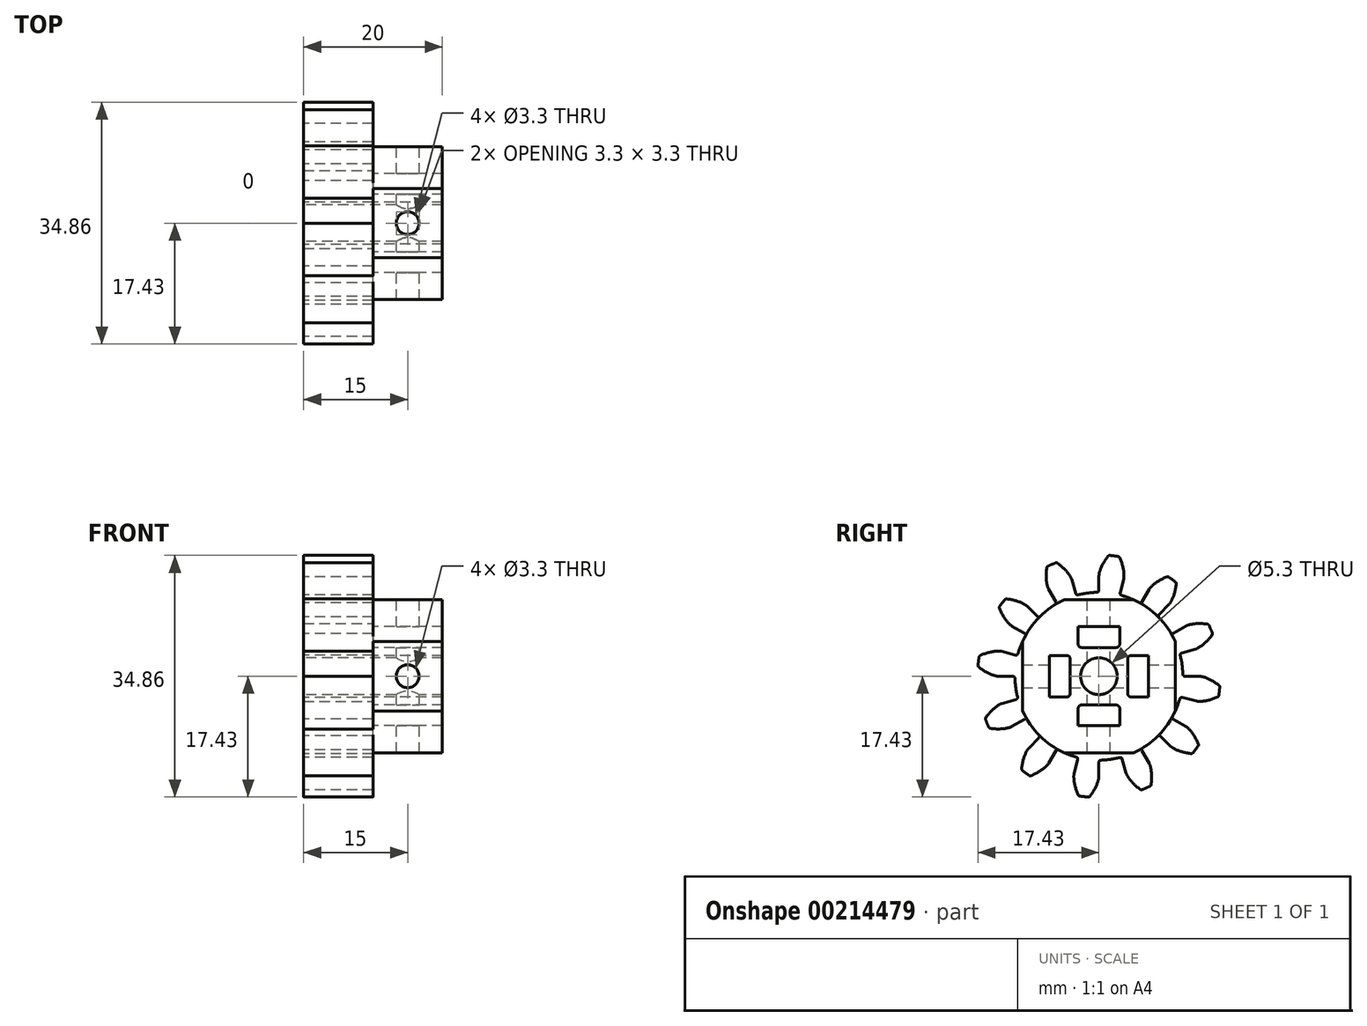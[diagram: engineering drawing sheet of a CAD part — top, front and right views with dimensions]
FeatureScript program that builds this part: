
annotation { "Feature Type Name" : "Feature", "Feature Type Description" : "" }
export const myFeature = defineFeature(function(context is Context, id is Id, definition is map)
    precondition{}
    {
        {
            assignVariable(context, id + "F0", {"name" : "NumberTeeth", "anyValue" : 12});
        }
        {
            assignVariable(context, id + "F1", {"name" : "GearThickness", "anyValue" : 10});
        }
        {
            var Q0;
            Q0=qCreatedBy(makeId("Right.planeOp"),FACE);
            var sketch = newSketch(context, id + "F2", { "sketchPlane" : qUnion([Q0])});
            skCircle(sketch, "E0", {"center": v(0, 0) * mm, "radius": 12.1 * mm});
            skCircle(sketch, "E1", {"center": v(0, 0) * mm, "radius": 14.52 * mm, "construction": true});
            skCircle(sketch, "E2", {"center": v(0, 0) * mm, "radius": 15 * mm, "construction": true});
            skCircle(sketch, "E3", {"center": v(0, 0) * mm, "radius": 17.5 * mm});
            skLineSegment(sketch, "E4", {"start": v(0, 0) * mm, "end": v(-14.52, 0) * mm, "construction": true});
            skLineSegment(sketch, "E5.1.0", {"start": v(0, 0) * mm, "end": v(-14.5, 0.73) * mm, "construction": true});
            skLineSegment(sketch, "E5.2.0", {"start": v(0, 0) * mm, "end": v(-14.45, 1.45) * mm, "construction": true});
            skLineSegment(sketch, "E5.3.0", {"start": v(0, 0) * mm, "end": v(-14.36, 2.17) * mm, "construction": true});
            skLineSegment(sketch, "E5.4.0", {"start": v(0, 0) * mm, "end": v(-14.23, 2.89) * mm, "construction": true});
            skLineSegment(sketch, "E5.5.0", {"start": v(0, 0) * mm, "end": v(-14.07, 3.6) * mm, "construction": true});
            skLineSegment(sketch, "E5.6.0", {"start": v(0, 0) * mm, "end": v(-13.87, 4.3) * mm, "construction": true});
            skLineSegment(sketch, "E5.7.0", {"start": v(0, 0) * mm, "end": v(-13.64, 4.98) * mm, "construction": true});
            skLineSegment(sketch, "E5.8.0", {"start": v(0, 0) * mm, "end": v(-13.38, 5.66) * mm, "construction": true});
            skLineSegment(sketch, "E5.9.0", {"start": v(0, 0) * mm, "end": v(-13.08, 6.32) * mm, "construction": true});
            skLineSegment(sketch, "E5.10.0", {"start": v(0, 0) * mm, "end": v(-12.74, 6.96) * mm, "construction": true});
            skLineSegment(sketch, "E5.11.0", {"start": v(0, 0) * mm, "end": v(-12.38, 7.6) * mm, "construction": true});
            skLineSegment(sketch, "E5.12.0", {"start": v(0, 0) * mm, "end": v(-11.99, 8.2) * mm, "construction": true});
            skLineSegment(sketch, "E5.13.0", {"start": v(0, 0) * mm, "end": v(-11.56, 8.79) * mm, "construction": true});
            skLineSegment(sketch, "E5.14.0", {"start": v(0, 0) * mm, "end": v(-11.1, 9.36) * mm, "construction": true});
            skLineSegment(sketch, "E5.anchor2", {"start": v(0, 0) * mm, "end": v(-11.1, 9.36) * mm, "construction": true});
            skLineSegment(sketch, "E6", {"start": v(-14.5, 0.73) * mm, "end": v(-14.54, 0) * mm, "construction": true});
            skLineSegment(sketch, "E7", {"start": v(-14.45, 1.45) * mm, "end": v(-14.6, 0) * mm, "construction": true});
            skLineSegment(sketch, "E8", {"start": v(-14.36, 2.17) * mm, "end": v(-14.68, 0.02) * mm, "construction": true});
            skLineSegment(sketch, "E9", {"start": v(-14.07, 3.6) * mm, "end": v(-14.97, 0.08) * mm, "construction": true});
            skLineSegment(sketch, "E10", {"start": v(-13.87, 4.3) * mm, "end": v(-15.16, 0.13) * mm, "construction": true});
            skLineSegment(sketch, "E11", {"start": v(-13.64, 4.98) * mm, "end": v(-15.38, 0.2) * mm, "construction": true});
            skLineSegment(sketch, "E12", {"start": v(-13.38, 5.66) * mm, "end": v(-15.64, 0.3) * mm, "construction": true});
            skLineSegment(sketch, "E13", {"start": v(-13.08, 6.32) * mm, "end": v(-15.92, 0.43) * mm, "construction": true});
            skLineSegment(sketch, "E14", {"start": v(-12.74, 6.96) * mm, "end": v(-16.23, 0.6) * mm, "construction": true});
            skLineSegment(sketch, "E15", {"start": v(-12.38, 7.6) * mm, "end": v(-16.56, 0.78) * mm, "construction": true});
            skLineSegment(sketch, "E16", {"start": v(-14.23, 2.89) * mm, "end": v(-14.8, 0.04) * mm, "construction": true});
            skLineSegment(sketch, "E17", {"start": v(-11.99, 8.2) * mm, "end": v(-16.9, 1) * mm, "construction": true});
            skLineSegment(sketch, "E18", {"start": v(-11.56, 8.79) * mm, "end": v(-17.27, 1.27) * mm, "construction": true});
            skLineSegment(sketch, "E19", {"start": v(-11.1, 9.36) * mm, "end": v(-17.66, 1.58) * mm, "construction": true});
            skLineSegment(sketch, "E20", {"start": v(0, 0) * mm, "end": v(-14.4, 1.8) * mm, "construction": true});
            skLineSegment(sketch, "E21", {"start": v(-12.1, 0) * mm, "end": v(-14.52, 0) * mm});
            skLineSegment(sketch, "E22.MirrorCS", {"start": v(-11.73, 2.99) * mm, "end": v(-14.07, 3.58) * mm});
            skLineSegment(sketch, "E23", {"start": v(-17.66, 1.58) * mm, "end": v(-17.84, 1.74) * mm, "construction": true});
            skFitSpline(sketch, "E24", {"points": [v(-17.66, 1.58) * mm, v(-17.27, 1.27) * mm, v(-16.9, 1) * mm, v(-16.56, 0.78) * mm, v(-16.23, 0.6) * mm, v(-15.92, 0.43) * mm, v(-15.64, 0.3) * mm, v(-15.38, 0.2) * mm, v(-15.16, 0.13) * mm, v(-14.97, 0.08) * mm, v(-14.8, 0.04) * mm, v(-14.68, 0.02) * mm, v(-14.6, 0) * mm, v(-14.54, 0) * mm, v(-14.52, 0) * mm], "startDerivative": vector(2.51, -2.05) * mm, "endDerivative": vector(1.04, 0) * mm});
            skFitSpline(sketch, "E25.MirrorCS", {"points": [v(-17.5, 2.83) * mm, v(-17.05, 3.03) * mm, v(-16.63, 3.2) * mm, v(-16.24, 3.33) * mm, v(-15.87, 3.43) * mm, v(-15.53, 3.5) * mm, v(-15.23, 3.56) * mm, v(-14.96, 3.6) * mm, v(-14.72, 3.62) * mm, v(-14.52, 3.62) * mm, v(-14.36, 3.62) * mm, v(-14.23, 3.6) * mm, v(-14.14, 3.6) * mm, v(-14.1, 3.59) * mm, v(-14.07, 3.58) * mm], "startDerivative": vector(2.94, 1.36) * mm, "endDerivative": vector(1.01, -0.26) * mm});
            skSolve(sketch);
        }
        {
            var Q0;
            {var subQ0=sQuery(id+"F2.wireOp",EDGE,"E0");var subQ27=makeQuery(id+"F2.imprint","INTERSECT",VERTEX,{"derivedFrom":[subQ0,sQuery(id+"F2.wireOp",EDGE,"10ea1024-8cf5-41f5-a75f-a634b86921f3.10.0")]});Q0=makeQuery(id+"F2.imprint","IMPRINT",FACE,{"disambiguationData":[TD([[makeQuery(id+"F2.imprint","IMPRINT",EDGE,{"disambiguationData":[TD([[subQ27,-1.0]])],"derivedFrom":subQ0}),1.0]])]});}
            var Q1;
            {var subQ0=sQuery(id+"F2.wireOp",EDGE,"10ea1024-8cf5-41f5-a75f-a634b86921f3.1.0");Q1=makeQuery(id+"F2.imprint","IMPRINT",FACE,{"disambiguationData":[TD([[makeQuery(id+"F2.imprint","IMPRINT",EDGE,{"derivedFrom":subQ0}),-1.0]])]});}
            var Q2;
            {var subQ7=sQuery(id+"F2.wireOp",EDGE,"10ea1024-8cf5-41f5-a75f-a634b86921f3.2.0");Q2=makeQuery(id+"F2.imprint","IMPRINT",FACE,{"disambiguationData":[TD([[makeQuery(id+"F2.imprint","IMPRINT",EDGE,{"derivedFrom":subQ7}),-1.0]])]});}
            var Q3;
            {var subQ8=sQuery(id+"F2.wireOp",EDGE,"10ea1024-8cf5-41f5-a75f-a634b86921f3.3.0");Q3=makeQuery(id+"F2.imprint","IMPRINT",FACE,{"disambiguationData":[TD([[makeQuery(id+"F2.imprint","IMPRINT",EDGE,{"derivedFrom":subQ8}),-1.0]])]});}
            var Q4;
            {var subQ2=sQuery(id+"F2.wireOp",EDGE,"10ea1024-8cf5-41f5-a75f-a634b86921f3.4.0");Q4=makeQuery(id+"F2.imprint","IMPRINT",FACE,{"disambiguationData":[TD([[makeQuery(id+"F2.imprint","IMPRINT",EDGE,{"derivedFrom":subQ2}),-1.0]])]});}
            var Q5;
            {var subQ8=sQuery(id+"F2.wireOp",EDGE,"10ea1024-8cf5-41f5-a75f-a634b86921f3.5.0");Q5=makeQuery(id+"F2.imprint","IMPRINT",FACE,{"disambiguationData":[TD([[makeQuery(id+"F2.imprint","IMPRINT",EDGE,{"derivedFrom":subQ8}),-1.0]])]});}
            var Q6;
            {var subQ3=sQuery(id+"F2.wireOp",EDGE,"10ea1024-8cf5-41f5-a75f-a634b86921f3.6.0");Q6=makeQuery(id+"F2.imprint","IMPRINT",FACE,{"disambiguationData":[TD([[makeQuery(id+"F2.imprint","IMPRINT",EDGE,{"derivedFrom":subQ3}),-1.0]])]});}
            var Q7;
            {var subQ0=sQuery(id+"F2.wireOp",EDGE,"10ea1024-8cf5-41f5-a75f-a634b86921f3.7.0");Q7=makeQuery(id+"F2.imprint","IMPRINT",FACE,{"disambiguationData":[TD([[makeQuery(id+"F2.imprint","IMPRINT",EDGE,{"derivedFrom":subQ0}),-1.0]])]});}
            var Q8;
            {var subQ5=sQuery(id+"F2.wireOp",EDGE,"10ea1024-8cf5-41f5-a75f-a634b86921f3.8.0");Q8=makeQuery(id+"F2.imprint","IMPRINT",FACE,{"disambiguationData":[TD([[makeQuery(id+"F2.imprint","IMPRINT",EDGE,{"derivedFrom":subQ5}),-1.0]])]});}
            var Q9;
            {var subQ1=sQuery(id+"F2.wireOp",EDGE,"10ea1024-8cf5-41f5-a75f-a634b86921f3.9.0");Q9=makeQuery(id+"F2.imprint","IMPRINT",FACE,{"disambiguationData":[TD([[makeQuery(id+"F2.imprint","IMPRINT",EDGE,{"derivedFrom":subQ1}),-1.0]])]});}
            var Q10;
            {var subQ5=sQuery(id+"F2.wireOp",EDGE,"10ea1024-8cf5-41f5-a75f-a634b86921f3.10.0");Q10=makeQuery(id+"F2.imprint","IMPRINT",FACE,{"disambiguationData":[TD([[makeQuery(id+"F2.imprint","IMPRINT",EDGE,{"derivedFrom":subQ5}),-1.0]])]});}
            var Q11;
            {var subQ8=sQuery(id+"F2.wireOp",EDGE,"10ea1024-8cf5-41f5-a75f-a634b86921f3.11.0");Q11=makeQuery(id+"F2.imprint","IMPRINT",FACE,{"disambiguationData":[TD([[makeQuery(id+"F2.imprint","IMPRINT",EDGE,{"derivedFrom":subQ8}),-1.0]])]});}
            var Q12;
            {var subQ2=sQuery(id+"F2.wireOp",EDGE,"10ea1024-8cf5-41f5-a75f-a634b86921f3.12.0");Q12=makeQuery(id+"F2.imprint","IMPRINT",FACE,{"disambiguationData":[TD([[makeQuery(id+"F2.imprint","IMPRINT",EDGE,{"derivedFrom":subQ2}),-1.0]])]});}
            var Q13;
            {var subQ3=sQuery(id+"F2.wireOp",EDGE,"10ea1024-8cf5-41f5-a75f-a634b86921f3.13.0");Q13=makeQuery(id+"F2.imprint","IMPRINT",FACE,{"disambiguationData":[TD([[makeQuery(id+"F2.imprint","IMPRINT",EDGE,{"derivedFrom":subQ3}),-1.0]])]});}
            var Q14;
            {var subQ0=sQuery(id+"F2.wireOp",EDGE,"10ea1024-8cf5-41f5-a75f-a634b86921f3.14.0");Q14=makeQuery(id+"F2.imprint","IMPRINT",FACE,{"disambiguationData":[TD([[makeQuery(id+"F2.imprint","IMPRINT",EDGE,{"derivedFrom":subQ0}),-1.0]])]});}
            var Q15;
            {var subQ6=sQuery(id+"F2.wireOp",EDGE,"10ea1024-8cf5-41f5-a75f-a634b86921f3.15.0");Q15=makeQuery(id+"F2.imprint","IMPRINT",FACE,{"disambiguationData":[TD([[makeQuery(id+"F2.imprint","IMPRINT",EDGE,{"derivedFrom":subQ6}),-1.0]])]});}
            var Q16;
            {var subQ5=sQuery(id+"F2.wireOp",EDGE,"10ea1024-8cf5-41f5-a75f-a634b86921f3.16.0");Q16=makeQuery(id+"F2.imprint","IMPRINT",FACE,{"disambiguationData":[TD([[makeQuery(id+"F2.imprint","IMPRINT",EDGE,{"derivedFrom":subQ5}),-1.0]])]});}
            var Q17;
            {var subQ7=sQuery(id+"F2.wireOp",EDGE,"10ea1024-8cf5-41f5-a75f-a634b86921f3.17.0");Q17=makeQuery(id+"F2.imprint","IMPRINT",FACE,{"disambiguationData":[TD([[makeQuery(id+"F2.imprint","IMPRINT",EDGE,{"derivedFrom":subQ7}),-1.0]])]});}
            var Q18;
            {var subQ5=sQuery(id+"F2.wireOp",EDGE,"10ea1024-8cf5-41f5-a75f-a634b86921f3.18.0");Q18=makeQuery(id+"F2.imprint","IMPRINT",FACE,{"disambiguationData":[TD([[makeQuery(id+"F2.imprint","IMPRINT",EDGE,{"derivedFrom":subQ5}),-1.0]])]});}
            var Q19;
            {var subQ8=sQuery(id+"F2.wireOp",EDGE,"10ea1024-8cf5-41f5-a75f-a634b86921f3.19.0");Q19=makeQuery(id+"F2.imprint","IMPRINT",FACE,{"disambiguationData":[TD([[makeQuery(id+"F2.imprint","IMPRINT",EDGE,{"derivedFrom":subQ8}),-1.0]])]});}
            var Q20;
            {var subQ8=sQuery(id+"F2.wireOp",EDGE,"E21");Q20=makeQuery(id+"F2.imprint","IMPRINT",FACE,{"disambiguationData":[TD([[makeQuery(id+"F2.imprint","IMPRINT",EDGE,{"derivedFrom":subQ8}),-1.0]])]});}
            extrude(context, id + "F3", {"entities" : qUnion([Q0, Q1, Q2, Q3, Q4, Q5, Q6, Q7, Q8, Q9, Q10, Q11, Q12, Q13, Q14, Q15, Q16, Q17, Q18, Q19, Q20]), "depth" : (getVariable(context, 'GearThickness')) * mm});
        }
        {
            var Q0;
            Q0=makeQuery(id+"F3.opExtrude","SWEPT_EDGE",EDGE,{"disambiguationData":[OSD([sQuery(id+"F2.wireOp",EDGE,"E0"),sQuery(id+"F2.wireOp",EDGE,"E22.MirrorCS")])]});
            var Q1;
            Q1=makeQuery(id+"F3.opExtrude","SWEPT_EDGE",EDGE,{"disambiguationData":[OSD([sQuery(id+"F2.wireOp",EDGE,"E3"),sQuery(id+"F2.wireOp",EDGE,"E25.MirrorCS")])]});
            var Q2;
            Q2=makeQuery(id+"F3.opExtrude","SWEPT_EDGE",EDGE,{"disambiguationData":[OSD([sQuery(id+"F2.wireOp",EDGE,"E3"),sQuery(id+"F2.wireOp",EDGE,"E24")])]});
            var Q3;
            Q3=makeQuery(id+"F3.opExtrude","SWEPT_EDGE",EDGE,{"disambiguationData":[OSD([sQuery(id+"F2.wireOp",EDGE,"E0"),sQuery(id+"F2.wireOp",EDGE,"E21")])]});
            fillet(context, id + "F4", {"entities" : qUnion([Q0, Q1, Q2, Q3]), "radius" : 0.3 * mm, "tangentPropagation" : true, "allowEdgeOverflow" : false});
        }
        {
            var Q0;
            Q0=makeQuery(id+"F3.opExtrude","SWEPT_FACE",FACE,{"disambiguationData":[OSD([sQuery(id+"F2.wireOp",EDGE,"E22.MirrorCS")])]});
            var Q1;
            Q1=makeQuery(id+"F3.opExtrude","SWEPT_FACE",FACE,{"disambiguationData":[OSD([sQuery(id+"F2.wireOp",EDGE,"E25.MirrorCS")])]});
            var Q2;
            Q2=makeQuery(id+"F3.opExtrude","SWEPT_FACE",FACE,{"disambiguationData":[OSD([sQuery(id+"F2.wireOp",EDGE,"E3")])]});
            var Q3;
            Q3=makeQuery(id+"F3.opExtrude","SWEPT_FACE",FACE,{"disambiguationData":[OSD([sQuery(id+"F2.wireOp",EDGE,"E24")])]});
            var Q4;
            Q4=makeQuery(id+"F3.opExtrude","SWEPT_FACE",FACE,{"disambiguationData":[OSD([sQuery(id+"F2.wireOp",EDGE,"E21")])]});
            var Q5;
            Q5=makeQuery(id+"F4.opFillet","BLEND_FACE",FACE,{"disambiguationData":[OSD([sQuery(id+"F2.wireOp",EDGE,"E0"),sQuery(id+"F2.wireOp",EDGE,"E22.MirrorCS")])]});
            var Q6;
            Q6=makeQuery(id+"F4.opFillet","BLEND_FACE",FACE,{"disambiguationData":[OSD([sQuery(id+"F2.wireOp",EDGE,"E3"),sQuery(id+"F2.wireOp",EDGE,"E25.MirrorCS")])]});
            var Q7;
            Q7=makeQuery(id+"F4.opFillet","BLEND_FACE",FACE,{"disambiguationData":[OSD([sQuery(id+"F2.wireOp",EDGE,"E3"),sQuery(id+"F2.wireOp",EDGE,"E24")])]});
            var Q8;
            Q8=makeQuery(id+"F4.opFillet","BLEND_FACE",FACE,{"disambiguationData":[OSD([sQuery(id+"F2.wireOp",EDGE,"E0"),sQuery(id+"F2.wireOp",EDGE,"E21")])]});
            var Q9;
            Q9=makeQuery(id+"F3.opExtrude","SWEPT_FACE",FACE,{"disambiguationData":[OSD([sQuery(id+"F2.wireOp",EDGE,"E0")])]});
            circularPattern(context, id + "F5", {"faces" : qUnion([Q0, Q1, Q2, Q3, Q4, Q5, Q6, Q7, Q8]), "axis" : qUnion([Q9]), "angle" : 360 * degree, "instanceCount" : getVariable(context, 'NumberTeeth'), "equalSpace" : true, "patternType" : PatternType.FACE});
        }
        {
            var Q0;
            Q0=makeQuery(id+"F3.opExtrude","CAP_FACE",FACE,{"disambiguationData":[OSD([sQuery(id+"F2.wireOp",EDGE,"E0"),sQuery(id+"F2.wireOp",EDGE,"E3"),sQuery(id+"F2.wireOp",EDGE,"E21"),sQuery(id+"F2.wireOp",EDGE,"E22.MirrorCS"),sQuery(id+"F2.wireOp",EDGE,"E24"),sQuery(id+"F2.wireOp",EDGE,"E25.MirrorCS")])],"isStart":false});
            var sketch = newSketch(context, id + "F6", { "sketchPlane" : qUnion([Q0])});
            skCircle(sketch, "E26", {"center": v(0, 0) * mm, "radius": 2.65 * mm});
            skCircle(sketch, "E27", {"center": v(0, 0) * mm, "radius": 12.1 * mm});
            skLineSegment(sketch, "E28", {"start": v(-12.1, 0) * mm, "end": v(12.1, 0) * mm, "construction": true});
            skLineSegment(sketch, "E29", {"start": v(-5, 11.03) * mm, "end": v(5, 11.03) * mm});
            skLineSegment(sketch, "E30.MirrorCS", {"start": v(-5, -11.03) * mm, "end": v(5, -11.03) * mm});
            skLineSegment(sketch, "E31", {"start": v(-11.03, 5) * mm, "end": v(-11.03, -5) * mm});
            skLineSegment(sketch, "E32", {"start": v(0, 12.1) * mm, "end": v(0, -12.1) * mm, "construction": true});
            skLineSegment(sketch, "E33.MirrorCS", {"start": v(11.03, 5) * mm, "end": v(11.03, -5) * mm});
            skLineSegment(sketch, "E34.bottom", {"start": v(3, 7.15) * mm, "end": v(-3, 7.15) * mm});
            skLineSegment(sketch, "E34.top", {"start": v(3, 4.15) * mm, "end": v(-3, 4.15) * mm});
            skLineSegment(sketch, "E34.left", {"start": v(3, 7.15) * mm, "end": v(3, 4.15) * mm});
            skLineSegment(sketch, "E34.right", {"start": v(-3, 7.15) * mm, "end": v(-3, 4.15) * mm});
            skPoint(sketch, "E34.middle", {"position": v(0, 5.65) * mm});
            skPoint(sketch, "E35.cornerSnap0", {"position": v(-13.05, 3.32) * mm});
            skLineSegment(sketch, "E36.bottom", {"start": v(-7.15, 3) * mm, "end": v(-4.15, 3) * mm});
            skLineSegment(sketch, "E36.top", {"start": v(-7.15, -3) * mm, "end": v(-4.15, -3) * mm});
            skLineSegment(sketch, "E36.left", {"start": v(-7.15, 3) * mm, "end": v(-7.15, -3) * mm});
            skLineSegment(sketch, "E36.right", {"start": v(-4.15, 3) * mm, "end": v(-4.15, -3) * mm});
            skPoint(sketch, "E36.middle", {"position": v(-5.65, 0) * mm});
            skLineSegment(sketch, "E37.MirrorCS", {"start": v(4.15, 3) * mm, "end": v(4.15, -3) * mm});
            skLineSegment(sketch, "E38.MirrorCS", {"start": v(7.15, 3) * mm, "end": v(4.15, 3) * mm});
            skLineSegment(sketch, "E39.MirrorCS", {"start": v(7.15, 3) * mm, "end": v(7.15, -3) * mm});
            skLineSegment(sketch, "E40.MirrorCS", {"start": v(7.15, -3) * mm, "end": v(4.15, -3) * mm});
            skLineSegment(sketch, "E41.MirrorCS", {"start": v(3, -4.15) * mm, "end": v(-3, -4.15) * mm});
            skLineSegment(sketch, "E42.MirrorCS", {"start": v(3, -7.15) * mm, "end": v(3, -4.15) * mm});
            skLineSegment(sketch, "E43.MirrorCS", {"start": v(3, -7.15) * mm, "end": v(-3, -7.15) * mm});
            skLineSegment(sketch, "E44.MirrorCS", {"start": v(-3, -7.15) * mm, "end": v(-3, -4.15) * mm});
            skSolve(sketch);
        }
        {
            var Q0;
            {var subQ0=sQuery(id+"F6.wireOp",EDGE,"E34.top");var subQ1=sQuery(id+"F6.wireOp",EDGE,"E26");var subQ2=makeQuery(id+"F6.imprint","INTERSECT",VERTEX,{"derivedFrom":[subQ1,subQ0]});Q0=makeQuery(id+"F6.imprint","IMPRINT",FACE,{"disambiguationData":[TD([[makeQuery(id+"F6.imprint","IMPRINT",EDGE,{"disambiguationData":[TD([[subQ2,-1.0]])],"derivedFrom":subQ1}),-1.0]])]});}
            var Q1;
            {var subQ12=sQuery(id+"F6.wireOp",EDGE,"E29");Q1=makeQuery(id+"F6.imprint","IMPRINT",FACE,{"disambiguationData":[TD([[makeQuery(id+"F6.imprint","IMPRINT",EDGE,{"derivedFrom":subQ12}),-1.0]])]});}
            extrude(context, id + "F7", {"entities" : qUnion([Q0, Q1]), "operationType" : NewBodyOperationType.ADD, "depth" : 10 * mm});
        }
        {
            var Q0;
            Q0=makeQuery(id+"F7.opExtrude","SWEPT_FACE",FACE,{"disambiguationData":[OSD([sQuery(id+"F6.wireOp",EDGE,"E29")])]});
            var sketch = newSketch(context, id + "F8", { "sketchPlane" : qUnion([Q0])});
            skPoint(sketch, "E45", {"position": v(15, 0) * mm});
            skSolve(sketch);
        }
        {
            var Q0;
            Q0=makeQuery(id+"F7.opExtrude","SWEPT_FACE",FACE,{"disambiguationData":[OSD([sQuery(id+"F6.wireOp",EDGE,"E33.MirrorCS")])]});
            var sketch = newSketch(context, id + "F9", { "sketchPlane" : qUnion([Q0])});
            skPoint(sketch, "E46", {"position": v(-15, 0) * mm});
            skPoint(sketch, "E47", {"position": v(-15, 5) * mm});
            skPoint(sketch, "E48", {"position": v(-20, 0) * mm});
            skSolve(sketch);
        }
        {
            var Q0;
            Q0=sQuery(id+"F9.wireOp",VERTEX,"E46");
            var Q1;
            Q1=sQuery(id+"F8.wireOp",VERTEX,"E45");
            var Q2;
            Q2=makeQuery(id+"F3.opExtrude","SWEPT_BODY",BODY,{"disambiguationData":[OSD([sQuery(id+"F2.wireOp",EDGE,"E0"),sQuery(id+"F2.wireOp",EDGE,"E3"),sQuery(id+"F2.wireOp",EDGE,"E21"),sQuery(id+"F2.wireOp",EDGE,"E22.MirrorCS"),sQuery(id+"F2.wireOp",EDGE,"E24"),sQuery(id+"F2.wireOp",EDGE,"E25.MirrorCS")])]});
            hole(context, id + "F10", {"style" : HoleStyle.SIMPLE, "endStyle" : HoleEndStyle.THROUGH, "standardTappedOrClearance" : lookupTablePath({ "standard" : "ISO", "fit" : "Normal", "size" : "M3", "type" : "Clearance" }), "standardBlindInLast" : lookupTablePath({ "fit" : "Standard", "standard" : "ISO", "size" : "M3", "type" : "Clearance" }), "holeDiameter" : 3.3 * mm, "locations" : qUnion([Q0, Q1]), "scope" : qUnion([Q2]), "isTappedThrough" : true});
        }
        {
            var Q0;
            Q0=makeQuery(id+"F7.opExtrude","SWEPT_EDGE",EDGE,{"disambiguationData":[OSD([sQuery(id+"F6.wireOp",EDGE,"E37.MirrorCS"),sQuery(id+"F6.wireOp",EDGE,"E40.MirrorCS")])]});
            var Q1;
            Q1=makeQuery(id+"F7.opExtrude","SWEPT_EDGE",EDGE,{"disambiguationData":[OSD([sQuery(id+"F6.wireOp",EDGE,"E37.MirrorCS"),sQuery(id+"F6.wireOp",EDGE,"E38.MirrorCS")])]});
            var Q2;
            Q2=makeQuery(id+"F7.opExtrude","SWEPT_EDGE",EDGE,{"disambiguationData":[OSD([sQuery(id+"F6.wireOp",EDGE,"E41.MirrorCS"),sQuery(id+"F6.wireOp",EDGE,"E42.MirrorCS")])]});
            var Q3;
            Q3=makeQuery(id+"F7.opExtrude","SWEPT_EDGE",EDGE,{"disambiguationData":[OSD([sQuery(id+"F6.wireOp",EDGE,"E41.MirrorCS"),sQuery(id+"F6.wireOp",EDGE,"E44.MirrorCS")])]});
            var Q4;
            Q4=makeQuery(id+"F7.opExtrude","SWEPT_EDGE",EDGE,{"disambiguationData":[OSD([sQuery(id+"F6.wireOp",EDGE,"E34.top"),sQuery(id+"F6.wireOp",EDGE,"E34.right")])]});
            var Q5;
            Q5=makeQuery(id+"F7.opExtrude","SWEPT_EDGE",EDGE,{"disambiguationData":[OSD([sQuery(id+"F6.wireOp",EDGE,"E34.top"),sQuery(id+"F6.wireOp",EDGE,"E34.left")])]});
            var Q6;
            Q6=makeQuery(id+"F7.opExtrude","SWEPT_EDGE",EDGE,{"disambiguationData":[OSD([sQuery(id+"F6.wireOp",EDGE,"E36.top"),sQuery(id+"F6.wireOp",EDGE,"E36.right")])]});
            var Q7;
            Q7=makeQuery(id+"F7.opExtrude","SWEPT_EDGE",EDGE,{"disambiguationData":[OSD([sQuery(id+"F6.wireOp",EDGE,"E36.bottom"),sQuery(id+"F6.wireOp",EDGE,"E36.right")])]});
            fillet(context, id + "F11", {"entities" : qUnion([Q0, Q1, Q2, Q3, Q4, Q5, Q6, Q7]), "radius" : 0.5 * mm, "tangentPropagation" : true, "allowEdgeOverflow" : false});
        }
        {
            var Q0;
            Q0=makeQuery(id+"F7.boolean.opBoolean","SPLIT",FACE,{"disambiguationData":[TD([makeQuery(id+"F7.opExtrude","SWEPT_FACE",FACE,{"disambiguationData":[OSD([sQuery(id+"F6.wireOp",EDGE,"E26")])]})])],"derivedFrom":makeQuery(id+"F3.opExtrude","CAP_FACE",FACE,{"disambiguationData":[OSD([sQuery(id+"F2.wireOp",EDGE,"E0"),sQuery(id+"F2.wireOp",EDGE,"E3"),sQuery(id+"F2.wireOp",EDGE,"E21"),sQuery(id+"F2.wireOp",EDGE,"E22.MirrorCS"),sQuery(id+"F2.wireOp",EDGE,"E24"),sQuery(id+"F2.wireOp",EDGE,"E25.MirrorCS")])],"isStart":false})});
            extrude(context, id + "F12", {"entities" : qUnion([Q0]), "operationType" : NewBodyOperationType.REMOVE, "endBound" : BoundingType.THROUGH_ALL, "oppositeDirection" : true, "depth" : 25 * mm});
        }
    });
